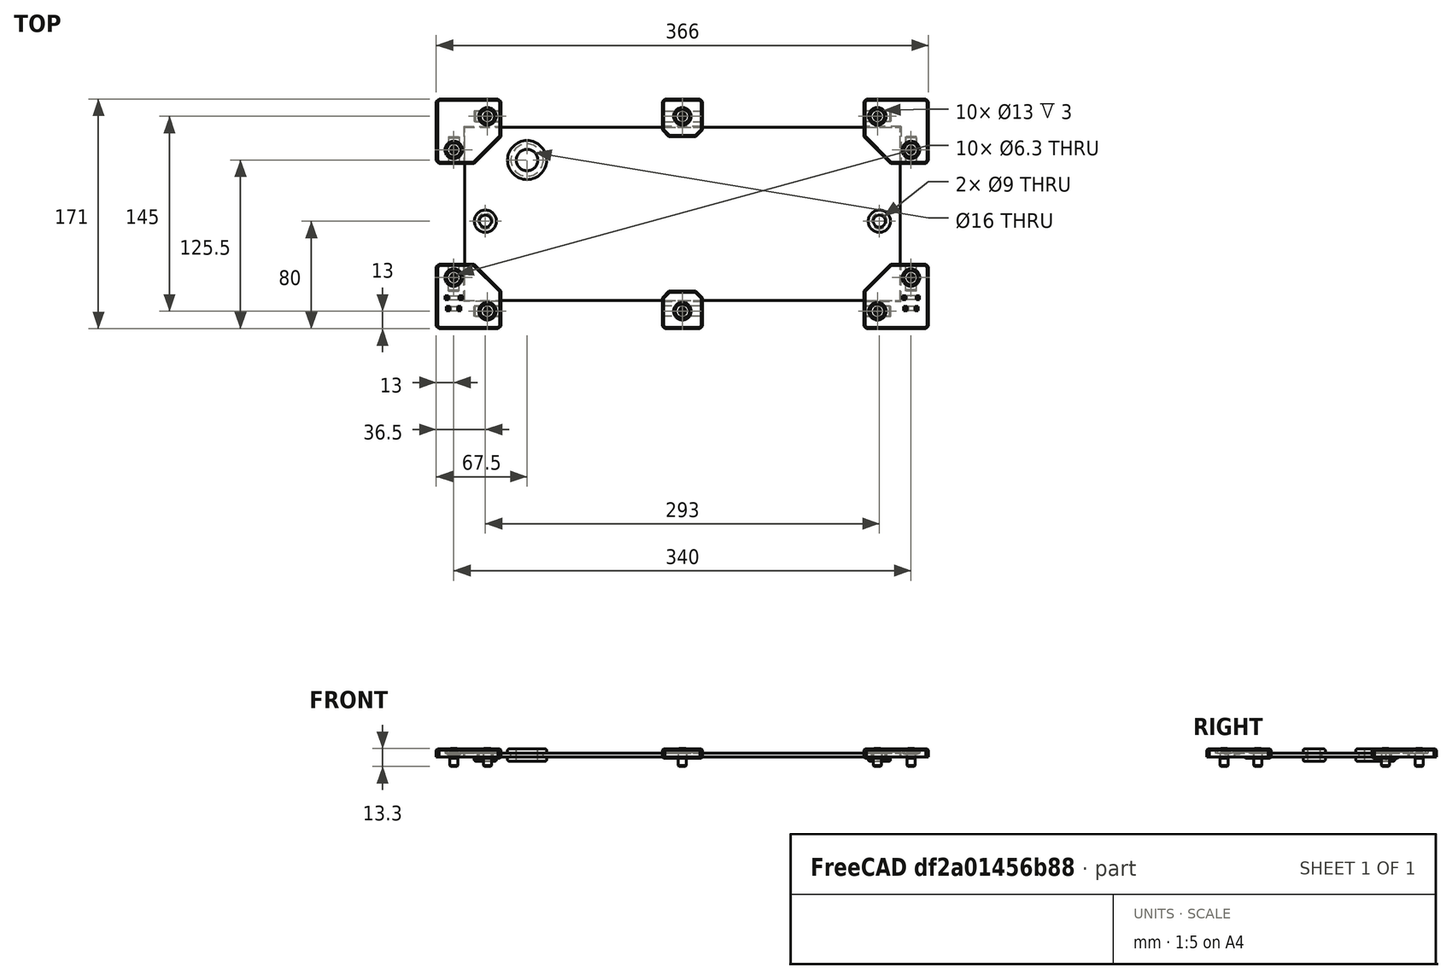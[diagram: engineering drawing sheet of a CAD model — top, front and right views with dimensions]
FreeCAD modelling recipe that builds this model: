
FCSTD DOCUMENT  (FreeCAD 0.19R24291 (Git))
Label: back-top-panel-assembly
License: Other
LicenseURL: GPL3
objects: Part::FeaturePython×10, Part::Feature×9, Part::Box×1, App::Part×1
note: 20 computed .brp shape members not serialized (recipe doc carries the construction recipe); baked Part::Feature solids carry a one-line shape summary decoded from their .brp

FEATURE [Part::Box] Box  label="panel-324x129x3mm"
  AttacherType = Attacher::AttachEngine3D
  Height = 3
  Length = 324
  Placement = pos=(-162,-64.5,0) rot=(0,0,1;0rad)
  Width = 129
FEATURE [Part::Feature] Cut002008006003  label="side-corner-panel-clip003"
  Placement = pos=(155,57.5,1.1e-14) rot=(0,0.707107,-0.707107;3.14159rad)
  shape: bbox 48 x 48 x 7 mm, 37 faces (baked)
FEATURE [Part::Feature] Cut002008006004  label="side-corner-panel-clip004"
  Placement = pos=(-155,57.5,1.1e-14) rot=(0.57735,-0.57735,0.57735;4.18879rad)
  shape: bbox 48 x 48 x 7 mm, 37 faces (baked)
FEATURE [Part::FeaturePython] Screw  label="M6x10-Screw"  # Fasteners workbench fastener (typed FeaturePython)
  Placement = pos=(-170,-47.5,3) rot=(0,0,1;0rad)
  diameter = 4
  invert = true
  length = 0
  lengthCustom = 10
  matchOuter = true
  offset = 0
  thread = false
  type = 39
FEATURE [Part::FeaturePython] Screw001  label="M6x10-Screw023"  # Fasteners workbench fastener (typed FeaturePython)
  Placement = pos=(-145,-72.5,3) rot=(0,0,1;0rad)
  diameter = 4
  invert = true
  length = 0
  lengthCustom = 10
  matchOuter = true
  offset = 0
  thread = false
  type = 39
FEATURE [Part::FeaturePython] Screw002  label="M6x10-Screw020"  # Fasteners workbench fastener (typed FeaturePython)
  Placement = pos=(-7e-15,-72.5,3) rot=(0,0,1;0rad)
  diameter = 4
  invert = true
  length = 0
  lengthCustom = 10
  matchOuter = true
  offset = 0
  thread = false
  type = 39
FEATURE [Part::FeaturePython] Screw003  label="M6x10-Screw022"  # Fasteners workbench fastener (typed FeaturePython)
  Placement = pos=(145,-72.5,3) rot=(0,0,1;0rad)
  diameter = 4
  invert = true
  length = 0
  lengthCustom = 10
  matchOuter = true
  offset = 0
  thread = false
  type = 39
FEATURE [Part::FeaturePython] Screw004  label="M6x10-Screw021"  # Fasteners workbench fastener (typed FeaturePython)
  Placement = pos=(170,-47.5,3) rot=(0,0,1;0rad)
  diameter = 4
  invert = true
  length = 0
  lengthCustom = 10
  matchOuter = true
  offset = 0
  thread = false
  type = 39
FEATURE [Part::FeaturePython] Screw005  label="M6x10-Screw014"  # Fasteners workbench fastener (typed FeaturePython)
  Placement = pos=(170,47.5,3) rot=(0,0,1;0rad)
  baseObject = -> Cut002008006003 [Edge84]
  diameter = 4
  invert = true
  length = 0
  lengthCustom = 10
  matchOuter = true
  offset = 0
  thread = false
  type = 39
FEATURE [Part::FeaturePython] Screw006  label="M6x10-Screw015"  # Fasteners workbench fastener (typed FeaturePython)
  Placement = pos=(145,72.5,3) rot=(0,0,1;0rad)
  baseObject = -> Cut002008006003 [Edge85]
  diameter = 4
  invert = true
  length = 0
  lengthCustom = 10
  matchOuter = true
  offset = 0
  thread = false
  type = 39
FEATURE [Part::FeaturePython] Screw007  label="M6x10-Screw019"  # Fasteners workbench fastener (typed FeaturePython)
  Placement = pos=(-4e-15,72.5,3) rot=(0,0,1;0rad)
  diameter = 4
  invert = true
  length = 0
  lengthCustom = 10
  matchOuter = true
  offset = 0
  thread = false
  type = 39
FEATURE [Part::FeaturePython] Screw008  label="M6x10-Screw017"  # Fasteners workbench fastener (typed FeaturePython)
  Placement = pos=(-170,47.5,3) rot=(0,0,1;0rad)
  baseObject = -> Cut002008006004 [Edge85]
  diameter = 4
  invert = true
  length = 0
  lengthCustom = 10
  matchOuter = true
  offset = 0
  thread = false
  type = 39
FEATURE [Part::FeaturePython] Screw009  label="M6x10-Screw018"  # Fasteners workbench fastener (typed FeaturePython)
  Placement = pos=(-145,72.5,3) rot=(0,0,1;0rad)
  baseObject = -> Cut002008006004 [Edge84]
  diameter = 4
  invert = true
  length = 0
  lengthCustom = 10
  matchOuter = true
  offset = 0
  thread = false
  type = 39
FEATURE [Part::Feature] Cut002008006004001001  label="side-panel-clip-smaller"
  Placement = pos=(-15,57.5,6) rot=(0.57735,-0.57735,0.57735;4.18879rad)
  shape: bbox 30 x 28 x 7 mm, 29 faces (baked)
FEATURE [Part::Feature] Cut002008006004001002  label="side-panel-clip-smaller001"
  Placement = pos=(15,-57.5,6) rot=(0.57735,0.57735,-0.57735;4.18879rad)
  shape: bbox 30 x 28 x 7 mm, 29 faces (baked)
FEATURE [Part::Feature] Fillet001002001002  label="cable-grommet-small001"
  Placement = pos=(146.5,-5.5,-3) rot=(0,0,1;0rad)
  shape: bbox 17.86 x 17.86 x 9 mm, 14 faces (baked)
FEATURE [Part::Feature] Fillet001002001003  label="cable-grommet-small002"
  Placement = pos=(-146.5,-5.5,-3) rot=(0,0,1;0rad)
  shape: bbox 17.86 x 17.86 x 9 mm, 14 faces (baked)
FEATURE [Part::Feature] Fillet001002001004  label="cable-grommet-big001"
  Placement = pos=(-115.5,40,-3) rot=(0,0,1;0rad)
  shape: bbox 31.39 x 31.39 x 9 mm, 14 faces (baked)
FEATURE [Part::Feature] Part__Mirroring001  label="Chamfer004001 (Mirror #1)001"
  Placement = pos=(-170,-43,0) rot=(0,0,1;3.14159rad)
  shape: bbox 48 x 48 x 7 mm, 85 faces (baked)
FEATURE [Part::Feature] Chamfer004001
  Placement = pos=(170,-43,0) rot=(0,0,1;3.14159rad)
  shape: bbox 48 x 48 x 7 mm, 85 faces (baked)
FEATURE [App::Part] Part  label="back-top-panel"
  Group = -> [Box,Cut002008006003,Cut002008006004,Screw001,Screw,Screw002,Screw004,Screw003,Screw006,Screw005,Screw007,Screw009,Screw008,Cut002008006004001001,Cut002008006004001002,Fillet001002001002,Fillet001002001003,Fillet001002001004,Chamfer004001,Part__Mirroring001]
  Origin = -> Origin
